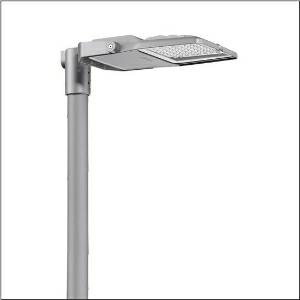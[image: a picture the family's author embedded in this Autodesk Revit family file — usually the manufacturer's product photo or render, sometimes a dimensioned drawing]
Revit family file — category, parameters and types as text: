
# Revit family: floodlight_fl_21_mini___pl61_5xa7771d2c3a_de69
name_source: partatom
category: Lighting Fixtures
units: mm (PartAtom-declared; Revit-internal decimal feet)

## family parameters
Cut with Voids When Loaded = No
Host = Face
Light Source = No
Part Type = Normal
Room Calculation Point = No
Round Connector Dimension = Use Diameter
Shared = No

## types (1)
- --- (1 x LED, 17500 lm, 143 W, 3000K)
    Apparent Load = 143 VA
    CIE Flux Codes = 33 65 98 100 100
    Color Rendering = 70
    Color Temperature = 3000K
    Default Elevation = 1800 mm
    Description = Floodlight FL 21 mini, floodlight, primary light control with lens, of PMMA, primary optical cover: protective disc, of toughened safety glass, transparent, light distribution: PL61, light emission: direct distribution, installation type: surface-mounted, LED, High Power LED, rated luminous flux: 17.500lm, luminous efficacy: 122lm/W, light colour: 730, colour temperature: 3000K, control gear: ECG iQ, control: Auto-Match, Temp-Guard, Lumen-Switch, Night-Set, Smart-Wire, Light-Fading, Desk-Remote (wireless, voltage-free reading and setting of iQ features in the workshop via application-optimized NFC function/RFID function), optimised constant luminous flux control (CLO 2.0), with terminal, 6-pole, mains connection: 220..240V, AC, 50/60Hz, start of lifetime: 143W, end of lifetime: 152W, reduction: 61W, luminaire housing, of diecast aluminium, powder-coated, Siteco® metallic grey (DB 702S), corrosivity category C5 according to DIN EN ISO 12944, mast bracket, of steel, galvanised, powder-coated, Siteco® metallic grey (DB 702S), protection rating (complete): IP66, insulation class (complete): insulation class II (safety insulation), certification: CE, ENEC, VDE, protection symbol: D, impact resistance: IK08, permissible operating ambient temperature: -40..+40°C, permissible operating ambient temperature for outdoor applications: -40..+50°C, standard: DIN EN 12944, packaging unit: 1 piece

Light Distribution: PL61
    Height = 70 mm
    Lamp = 1 x LED
    Lamp Light Flux = 17500 lm
    Lamp Power = 143 W
    Lamp count = 1
    Length = 485 mm
    Luminous efficacy = 122 lm/W
    Manufacturer = Siteco
    ModVariant = No
    Model = 5XA7771D2C3A
    Number of Poles = 1
    OnlyDefault = Yes
    Power Factor = 1
    Product Name = Floodlight FL 21 mini | PL61
    Product group = floodlight | pylon top
    ProductGroupID = 6101
    Protection Class = Protection class II
    Protection Degree = IP 66
    RLX_Detail_Level = 1
    RlxData = <blob elided: 101441 chars, md5=fdcf3c39>
    Socket = socket
    Standby Power = 0 W
    System Light Flux = 17500 lm
    System Power = 143 W
    Type Comments = factory setting: luminous flux: 100 % | dim-lin: 254 | 730 mA
    Type Image = l_1007125.jpg
    URL = http://relux.com
    VarID = @adj_085043
    Voltage = 0 V
    Weight = 0.00 kg
    Width = 337 mm

## geometry (parser evidence)
native form markers: Blend x4, Sweep x12
no freeform markers — native parametric forms only
